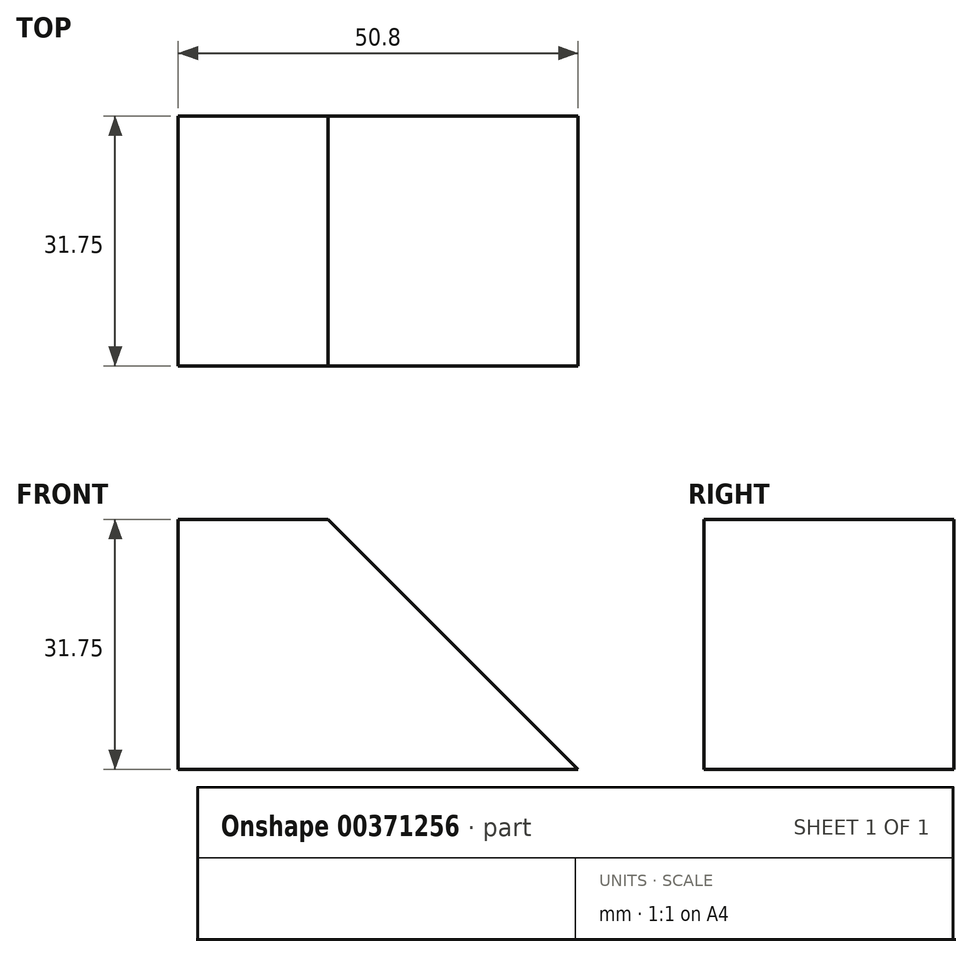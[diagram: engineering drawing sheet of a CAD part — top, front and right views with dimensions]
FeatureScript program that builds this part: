
annotation { "Feature Type Name" : "Feature", "Feature Type Description" : "" }
export const myFeature = defineFeature(function(context is Context, id is Id, definition is map)
    precondition{}
    {
        {
            var Q0;
            Q0=qCreatedBy(makeId("Front.planeOp"),FACE);
            var sketch = newSketch(context, id + "F0", { "sketchPlane" : qUnion([Q0])});
            skLineSegment(sketch, "E0", {"start": v(0, 31.75) * mm, "end": v(0, 0) * mm});
            skLineSegment(sketch, "E1", {"start": v(0, 0) * mm, "end": v(50.8, 0) * mm});
            skLineSegment(sketch, "E2", {"start": v(50.8, 0) * mm, "end": v(50.8, 31.75) * mm});
            skLineSegment(sketch, "E3", {"start": v(50.8, 31.75) * mm, "end": v(0, 31.75) * mm});
            skSolve(sketch);
        }
        {
            var Q0;
            Q0=makeQuery(id+"F0.imprint","IMPRINT",FACE,{"disambiguationData":[TD([[makeQuery(id+"F0.imprint","IMPRINT",EDGE,{"derivedFrom":sQuery(id+"F0.wireOp",EDGE,"E0")}),1.0]])]});
            extrude(context, id + "F1", {"entities" : qUnion([Q0]), "depth" : 31.75 * mm});
        }
        {
            var Q0;
            Q0=makeQuery(id+"F1.opExtrude","CAP_FACE",FACE,{"disambiguationData":[OSD([sQuery(id+"F0.wireOp",EDGE,"E0"),sQuery(id+"F0.wireOp",EDGE,"E1"),sQuery(id+"F0.wireOp",EDGE,"E2"),sQuery(id+"F0.wireOp",EDGE,"E3")])],"isStart":false});
            var sketch = newSketch(context, id + "F2", { "sketchPlane" : qUnion([Q0])});
            skLineSegment(sketch, "E4", {"start": v(19.05, 31.75) * mm, "end": v(50.8, 0) * mm});
            skSolve(sketch);
        }
        {
            var Q0;
            {var subQ0=sQuery(id+"F2.wireOp",EDGE,"E4");Q0=makeQuery(id+"F2.imprint","IMPRINT",FACE,{"disambiguationData":[TD([[makeQuery(id+"F2.imprint","IMPRINT",EDGE,{"derivedFrom":subQ0}),1.0]])]});}
            extrude(context, id + "F3", {"entities" : qUnion([Q0]), "operationType" : NewBodyOperationType.REMOVE, "oppositeDirection" : true, "depth" : 31.75 * mm});
        }
        {
            var Q0;
            Q0=makeQuery(id+"F3.boolean.opBoolean","COPY",FACE,{"derivedFrom":makeQuery(id+"F3.opExtrude","SWEPT_FACE",FACE,{"disambiguationData":[OSD([sQuery(id+"F2.wireOp",EDGE,"E4")])]})});
            var sketch = newSketch(context, id + "F4", { "sketchPlane" : qUnion([Q0])});
            skLineSegment(sketch, "E5", {"start": v(13.47, -31.75) * mm, "end": v(13.47, 0) * mm});
            skLineSegment(sketch, "E6", {"start": v(13.47, 0) * mm, "end": v(35.92, 0) * mm});
            skLineSegment(sketch, "E7", {"start": v(35.92, 0) * mm, "end": v(35.92, -31.75) * mm});
            skLineSegment(sketch, "E8", {"start": v(35.92, -31.75) * mm, "end": v(13.47, -31.75) * mm});
            skSolve(sketch);
        }
        {
            var Q0;
            Q0=makeQuery(id+"F4.imprint","IMPRINT",FACE,{"disambiguationData":[TD([[makeQuery(id+"F4.imprint","IMPRINT",EDGE,{"derivedFrom":sQuery(id+"F4.wireOp",EDGE,"E5")}),-1.0]])]});
            extrude(context, id + "F5", {"entities" : qUnion([Q0]), "operationType" : NewBodyOperationType.REMOVE, "depth" : 17.02 * mm});
        }
    });
